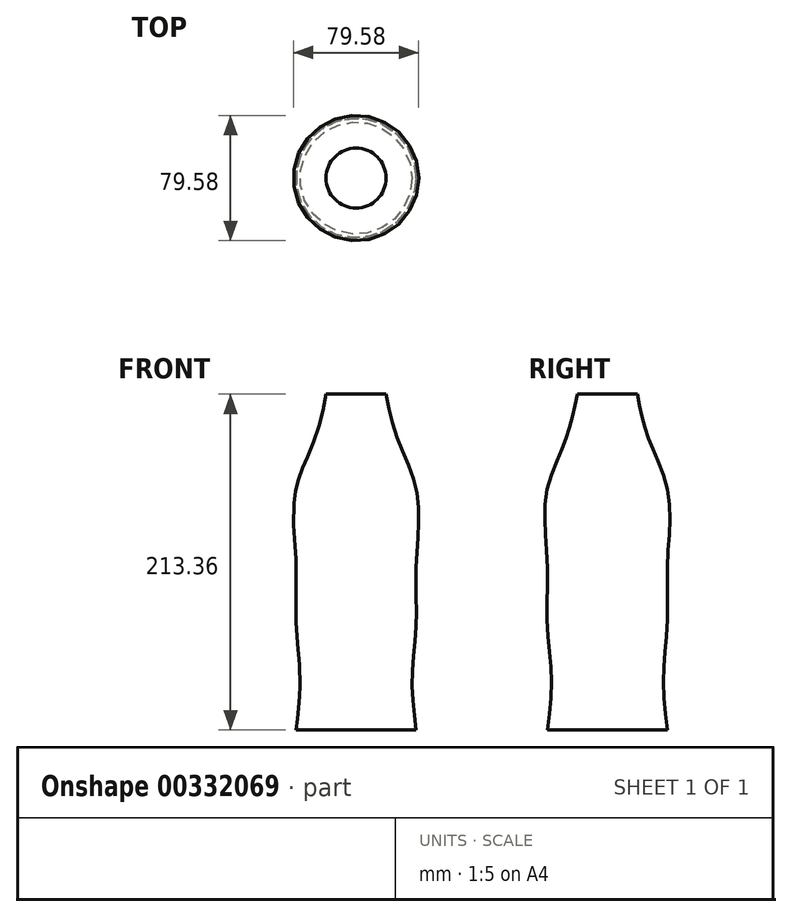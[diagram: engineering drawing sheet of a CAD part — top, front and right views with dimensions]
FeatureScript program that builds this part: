
annotation { "Feature Type Name" : "Feature", "Feature Type Description" : "" }
export const myFeature = defineFeature(function(context is Context, id is Id, definition is map)
    precondition{}
    {
        {
            var Q0;
            Q0=qCreatedBy(makeId("Top.planeOp"),FACE);
            cPlane(context, id + "F0", {"entities" : qUnion([Q0]), "cplaneType" : CPlaneType.OFFSET, "offset" : 48.77 * mm, "width" : 152.4 * mm, "height" : 152.4 * mm});
        }
        {
            var Q0;
            Q0=qCreatedBy(id+"F0.planeOp",FACE);
            cPlane(context, id + "F1", {"entities" : qUnion([Q0]), "cplaneType" : CPlaneType.OFFSET, "offset" : 33.78 * mm, "width" : 152.4 * mm, "height" : 152.4 * mm});
        }
        {
            var Q0;
            Q0=qCreatedBy(id+"F1.planeOp",FACE);
            cPlane(context, id + "F2", {"entities" : qUnion([Q0]), "cplaneType" : CPlaneType.OFFSET, "offset" : 25.9 * mm, "width" : 152.4 * mm, "height" : 152.4 * mm});
        }
        {
            var Q0;
            Q0=qCreatedBy(makeId("Top.planeOp"),FACE);
            cPlane(context, id + "F3", {"entities" : qUnion([Q0]), "cplaneType" : CPlaneType.OFFSET, "offset" : 38.1 * mm, "oppositeDirection" : true, "width" : 152.4 * mm, "height" : 152.4 * mm});
        }
        {
            var Q0;
            Q0=qCreatedBy(id+"F3.planeOp",FACE);
            cPlane(context, id + "F4", {"entities" : qUnion([Q0]), "cplaneType" : CPlaneType.OFFSET, "offset" : 33.78 * mm, "oppositeDirection" : true, "width" : 152.4 * mm, "height" : 152.4 * mm});
        }
        {
            var Q0;
            Q0=qCreatedBy(id+"F4.planeOp",FACE);
            cPlane(context, id + "F5", {"entities" : qUnion([Q0]), "cplaneType" : CPlaneType.OFFSET, "offset" : 33.02 * mm, "oppositeDirection" : true, "width" : 152.4 * mm, "height" : 152.4 * mm});
        }
        {
            var Q0;
            Q0=qCreatedBy(id+"F0.planeOp",FACE);
            var sketch = newSketch(context, id + "F6", { "sketchPlane" : qUnion([Q0])});
            skCircle(sketch, "E0", {"center": v(0, 0) * mm, "radius": 38.1 * mm});
            skSolve(sketch);
        }
        {
            var Q0;
            Q0=qCreatedBy(id+"F1.planeOp",FACE);
            var sketch = newSketch(context, id + "F7", { "sketchPlane" : qUnion([Q0])});
            skCircle(sketch, "E1", {"center": v(0, 0) * mm, "radius": 25.4 * mm});
            skSolve(sketch);
        }
        {
            var Q0;
            Q0=qCreatedBy(id+"F2.planeOp",FACE);
            var sketch = newSketch(context, id + "F8", { "sketchPlane" : qUnion([Q0])});
            skCircle(sketch, "E2", {"center": v(0, 0) * mm, "radius": 19.05 * mm});
            skSolve(sketch);
        }
        {
            var Q0;
            Q0=qCreatedBy(makeId("Top.planeOp"),FACE);
            var sketch = newSketch(context, id + "F9", { "sketchPlane" : qUnion([Q0])});
            skCircle(sketch, "E3", {"center": v(0, 0) * mm, "radius": 38.1 * mm});
            skSolve(sketch);
        }
        {
            var Q0;
            Q0=qCreatedBy(id+"F3.planeOp",FACE);
            var sketch = newSketch(context, id + "F10", { "sketchPlane" : qUnion([Q0])});
            skCircle(sketch, "E4", {"center": v(0, 0) * mm, "radius": 38.1 * mm});
            skSolve(sketch);
        }
        {
            var Q0;
            Q0=qCreatedBy(id+"F4.planeOp",FACE);
            var sketch = newSketch(context, id + "F11", { "sketchPlane" : qUnion([Q0])});
            skCircle(sketch, "E5", {"center": v(0, 0) * mm, "radius": 35.56 * mm});
            skSolve(sketch);
        }
        {
            var Q0;
            Q0=qCreatedBy(id+"F5.planeOp",FACE);
            var sketch = newSketch(context, id + "F12", { "sketchPlane" : qUnion([Q0])});
            skCircle(sketch, "E6", {"center": v(0, 0) * mm, "radius": 38.1 * mm});
            skSolve(sketch);
        }
        {
            var Q0;
            Q0=makeQuery(id+"F8.imprint","IMPRINT",FACE,{"disambiguationData":[TD([[makeQuery(id+"F8.imprint","IMPRINT",EDGE,{"derivedFrom":sQuery(id+"F8.wireOp",EDGE,"E2")}),1.0]])]});
            var Q1;
            Q1=makeQuery(id+"F7.imprint","IMPRINT",FACE,{"disambiguationData":[TD([[makeQuery(id+"F7.imprint","IMPRINT",EDGE,{"derivedFrom":sQuery(id+"F7.wireOp",EDGE,"E1")}),1.0]])]});
            var Q2;
            Q2=makeQuery(id+"F6.imprint","IMPRINT",FACE,{"disambiguationData":[TD([[makeQuery(id+"F6.imprint","IMPRINT",EDGE,{"derivedFrom":sQuery(id+"F6.wireOp",EDGE,"E0")}),1.0]])]});
            var Q3;
            Q3=makeQuery(id+"F9.imprint","IMPRINT",FACE,{"disambiguationData":[TD([[makeQuery(id+"F9.imprint","IMPRINT",EDGE,{"derivedFrom":sQuery(id+"F9.wireOp",EDGE,"E3")}),1.0]])]});
            var Q4;
            Q4=makeQuery(id+"F10.imprint","IMPRINT",FACE,{"disambiguationData":[TD([[makeQuery(id+"F10.imprint","IMPRINT",EDGE,{"derivedFrom":sQuery(id+"F10.wireOp",EDGE,"E4")}),1.0]])]});
            var Q5;
            Q5=makeQuery(id+"F11.imprint","IMPRINT",FACE,{"disambiguationData":[TD([[makeQuery(id+"F11.imprint","IMPRINT",EDGE,{"derivedFrom":sQuery(id+"F11.wireOp",EDGE,"E5")}),1.0]])]});
            var Q6;
            Q6=makeQuery(id+"F12.imprint","IMPRINT",FACE,{"disambiguationData":[TD([[makeQuery(id+"F12.imprint","IMPRINT",EDGE,{"derivedFrom":sQuery(id+"F12.wireOp",EDGE,"E6")}),1.0]])]});
            loft(context, id + "F13", {"sheetProfilesArray" : [{ "sheetProfileEntities" : qUnion([Q0]) }, { "sheetProfileEntities" : qUnion([Q1]) }, { "sheetProfileEntities" : qUnion([Q2]) }, { "sheetProfileEntities" : qUnion([Q3]) }, { "sheetProfileEntities" : qUnion([Q4]) }, { "sheetProfileEntities" : qUnion([Q5]) }, { "sheetProfileEntities" : qUnion([Q6]) }]});
        }
    });
